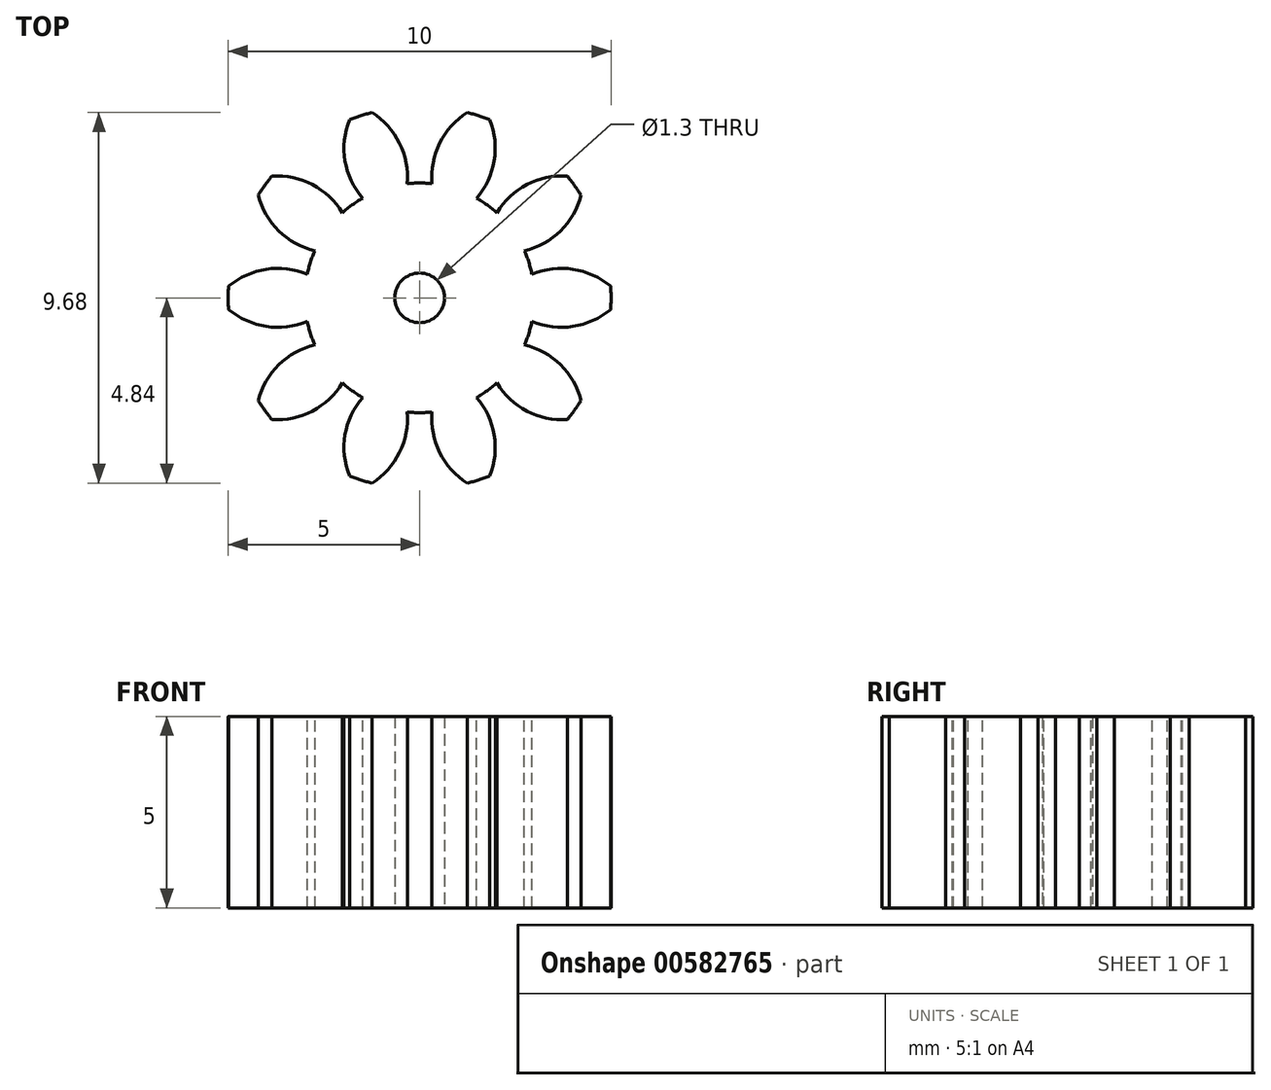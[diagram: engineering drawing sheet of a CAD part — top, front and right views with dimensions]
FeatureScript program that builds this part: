
annotation { "Feature Type Name" : "Feature", "Feature Type Description" : "" }
export const myFeature = defineFeature(function(context is Context, id is Id, definition is map)
    precondition{}
    {
        {
            var Q0;
            Q0=qCreatedBy(makeId("Top.planeOp"),FACE);
            var sketch = newSketch(context, id + "F0", { "sketchPlane" : qUnion([Q0])});
            skCircle(sketch, "E0", {"center": v(0, 0) * mm, "radius": 5 * mm});
            skCircle(sketch, "E1", {"center": v(0, 0) * mm, "radius": 0.65 * mm});
            skSolve(sketch);
        }
        {
            var Q0;
            Q0=makeQuery(id+"F0.imprint","IMPRINT",FACE,{"disambiguationData":[TD([[makeQuery(id+"F0.imprint","IMPRINT",EDGE,{"derivedFrom":sQuery(id+"F0.wireOp",EDGE,"E0")}),1.0]])]});
            extrude(context, id + "F1", {"entities" : qUnion([Q0]), "depth" : 5 * mm});
        }
        {
            var Q0;
            Q0=makeQuery(id+"F1.opExtrude","CAP_FACE",FACE,{"disambiguationData":[OSD([sQuery(id+"F0.wireOp",EDGE,"E0"),sQuery(id+"F0.wireOp",EDGE,"E1")])],"isStart":false});
            var sketch = newSketch(context, id + "F2", { "sketchPlane" : qUnion([Q0])});
            skCircle(sketch, "E2", {"center": v(0, 0) * mm, "radius": 3 * mm});
            skCircle(sketch, "E3", {"center": v(0, 0) * mm, "radius": 5 * mm});
            skArc(sketch, "E4", {"start": v(-0.32, 2.98) * mm, "mid": v(-0.53, 4.04) * mm, "end": v(-1.25, 4.84) * mm});
            skArc(sketch, "E5.MirrorCS", {"start": v(0.32, 2.98) * mm, "mid": v(0.53, 4.04) * mm, "end": v(1.25, 4.84) * mm});
            skSolve(sketch);
        }
        {
            var Q0;
            {var subQ0=sQuery(id+"F2.wireOp",EDGE,"E4");Q0=makeQuery(id+"F2.imprint","IMPRINT",FACE,{"disambiguationData":[TD([[makeQuery(id+"F2.imprint","IMPRINT",EDGE,{"derivedFrom":subQ0}),-1.0]])]});}
            extrude(context, id + "F3", {"entities" : qUnion([Q0]), "operationType" : NewBodyOperationType.REMOVE, "oppositeDirection" : true, "depth" : 25 * mm});
        }
        {
            var Q0;
            Q0=makeQuery(id+"F3.boolean.opBoolean","COPY",FACE,{"derivedFrom":makeQuery(id+"F3.opExtrude","SWEPT_FACE",FACE,{"disambiguationData":[OSD([sQuery(id+"F2.wireOp",EDGE,"E4")])]})});
            var Q1;
            Q1=makeQuery(id+"F3.boolean.opBoolean","COPY",FACE,{"derivedFrom":makeQuery(id+"F3.opExtrude","SWEPT_FACE",FACE,{"disambiguationData":[OSD([sQuery(id+"F2.wireOp",EDGE,"E2")])]})});
            var Q2;
            Q2=makeQuery(id+"F3.boolean.opBoolean","COPY",FACE,{"derivedFrom":makeQuery(id+"F3.opExtrude","SWEPT_FACE",FACE,{"disambiguationData":[OSD([sQuery(id+"F2.wireOp",EDGE,"E5.MirrorCS")])]})});
            var Q3;
            Q3=makeQuery(id+"F1.opExtrude","SWEPT_FACE",FACE,{"disambiguationData":[OSD([sQuery(id+"F0.wireOp",EDGE,"E0")])]});
            circularPattern(context, id + "F4", {"patternType" : PatternType.FACE, "faces" : qUnion([Q0, Q1, Q2]), "axis" : qUnion([Q3]), "angle" : 360 * degree, "instanceCount" : 10, "equalSpace" : true});
        }
    });
